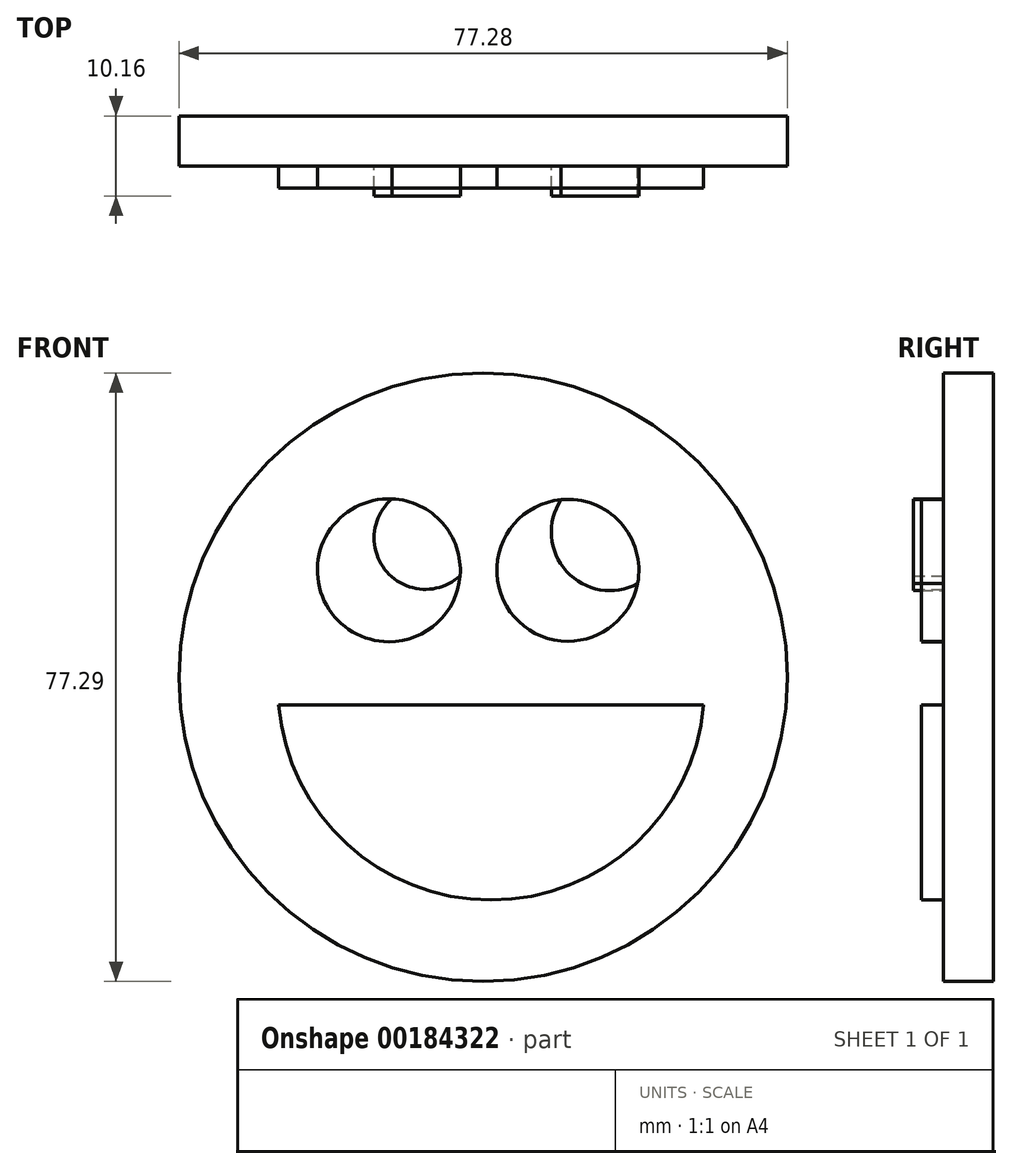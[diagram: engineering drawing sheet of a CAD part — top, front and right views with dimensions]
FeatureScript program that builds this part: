
annotation { "Feature Type Name" : "Feature", "Feature Type Description" : "" }
export const myFeature = defineFeature(function(context is Context, id is Id, definition is map)
    precondition{}
    {
        {
            var Q0;
            Q0=qCreatedBy(makeId("Front.planeOp"),FACE);
            var sketch = newSketch(context, id + "F0", { "sketchPlane" : qUnion([Q0])});
            skCircle(sketch, "E0", {"center": v(-24.9, 40.58) * mm, "radius": 9.08 * mm});
            skCircle(sketch, "E1", {"center": v(-2.15, 40.58) * mm, "radius": 9.02 * mm});
            skArc(sketch, "E2", {"start": v(-24.49, 49.64) * mm, "mid": v(-25.14, 40.36) * mm, "end": v(-15.85, 39.88) * mm});
            skArc(sketch, "E3", {"start": v(-3.03, 49.55) * mm, "mid": v(-2.32, 40.43) * mm, "end": v(6.7, 38.88) * mm});
            skLineSegment(sketch, "E4", {"start": v(-38.9, 23.48) * mm, "end": v(15.07, 23.48) * mm});
            skArc(sketch, "E5", {"start": v(-38.9, 23.48) * mm, "mid": v(-11.91, -1.31) * mm, "end": v(15.07, 23.48) * mm});
            skSolve(sketch);
        }
        {
            var Q0;
            {var subQ0=sQuery(id+"F0.wireOp",EDGE,"E2");Q0=makeQuery(id+"F0.imprint","IMPRINT",FACE,{"disambiguationData":[TD([[makeQuery(id+"F0.imprint","IMPRINT",EDGE,{"derivedFrom":subQ0}),1.0]])]});}
            var Q1;
            {var subQ0=sQuery(id+"F0.wireOp",EDGE,"E3");Q1=makeQuery(id+"F0.imprint","IMPRINT",FACE,{"disambiguationData":[TD([[makeQuery(id+"F0.imprint","IMPRINT",EDGE,{"derivedFrom":subQ0}),1.0]])]});}
            extrude(context, id + "F1", {"entities" : qUnion([Q0, Q1]), "depth" : 3.8 * mm});
        }
        {
            var Q0;
            Q0 = qSketchRegion(id + "F0", true);
            extrude(context, id + "F2", {"entities" : qUnion([Q0]), "depth" : 2.8 * mm});
        }
        {
            var Q0;
            Q0=qCreatedBy(makeId("Front.planeOp"),FACE);
            var sketch = newSketch(context, id + "F3", { "sketchPlane" : qUnion([Q0])});
            skCircle(sketch, "E6", {"center": v(-12.92, 26.98) * mm, "radius": 38.64 * mm});
            skSolve(sketch);
        }
        {
            var Q0;
            Q0=makeQuery(id+"F3.imprint","IMPRINT",FACE,{"disambiguationData":[TD([[makeQuery(id+"F3.imprint","IMPRINT",EDGE,{"derivedFrom":sQuery(id+"F3.wireOp",EDGE,"E6")}),1.0]])]});
            extrude(context, id + "F4", {"entities" : qUnion([Q0]), "oppositeDirection" : true, "depth" : 6.35 * mm});
        }
        {
            var Q0;
            Q0=makeQuery(id+"F2.opExtrude","CAP_FACE",FACE,{"disambiguationData":[OSD([sQuery(id+"F0.wireOp",EDGE,"E4"),sQuery(id+"F0.wireOp",EDGE,"E5")])],"isStart":false});
            var sketch = newSketch(context, id + "F5", { "sketchPlane" : qUnion([Q0])});
            skArc(sketch, "E7", {"start": v(8.82, 8.34) * mm, "mid": v(-2.3, 7.73) * mm, "end": v(-9, -1.16) * mm});
            skSolve(sketch);
        }
        {
            var Q0;
            {var subQ0=sQuery(id+"F5.wireOp",EDGE,"E7");Q0=makeQuery(id+"F5.imprint","IMPRINT",FACE,{"disambiguationData":[TD([[makeQuery(id+"F5.imprint","IMPRINT",EDGE,{"derivedFrom":subQ0}),1.0]])]});}
            extrude(context, id + "F6", {"entities" : qUnion([Q0]), "operationType" : NewBodyOperationType.ADD, "oppositeDirection" : true, "depth" : 1.27 * mm});
        }
    });
